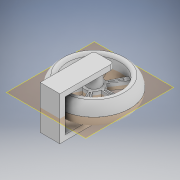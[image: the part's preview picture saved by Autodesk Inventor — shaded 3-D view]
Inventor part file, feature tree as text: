
AUTODESK INVENTOR PART (.ipt)
format: ipt  version: 2020 (Build 240168000, 168)  size: 317,952 bytes
history: native  units: mm
features: sketch x5, extrude x5, fillet x3, plane x1, mirror x1
ambient origin geometry x8: Origin, YZ Plane, XZ Plane, XY Plane, X Axis, Y Axis, Z Axis, Center Point
bodies: Solid1 (feature_tree)
feature tree (15):
  sketch  "Sketch1"  dims[d0=27.5mm d1=2.0mm]
  extrude  "Extrusion1"  Depth=2.0mm
  extrude  "Extrusion2"  Depth=5.0mm TaperAngle=360.0deg
  fillet  "Fillet1"  Radius=4.5mm
  sketch  "Sketch5"  dims[d18=6.0mm d19=60.0mm d21=360.0deg]
  fillet  "Fillet2"  Radius=5.0mm
  extrude  "Extrusion3"  Depth=60.0mm TaperAngle=360.0deg
  extrude  "Extrusion4"  Depth=10.0mm TaperAngle=0.0deg
  fillet  "Fillet3"  Radius=5.2mm
  extrude  "Extrusion5"  Depth=2.5mm
  plane  "Work Plane1"
  mirror  "Mirror1"
  sketch  "Sketch4"  dims[d8=0.5mm d9=0.5mm d10=60.0mm d12=360.0deg d14=4.5mm d17=5.0mm]
  sketch  "Sketch6"  dims[d23=2.5mm d24=0.0mm d25=10.0mm d26=0.0mm d27=5.2mm]
  sketch  "Sketch7"  dims[d28=7.0mm d29=2.5mm d30=1.0mm d31=5.0mm d32=0.0mm d33=7.5mm d34=7.5mm d35=11.0mm d36=7.5mm d37=2.0mm d38=2.0mm d39=0.0mm d40=1.0mm d41=2.0mm d42=6.26mm d43=0.0mm d15=0.5mm d16=0.872665mm]
